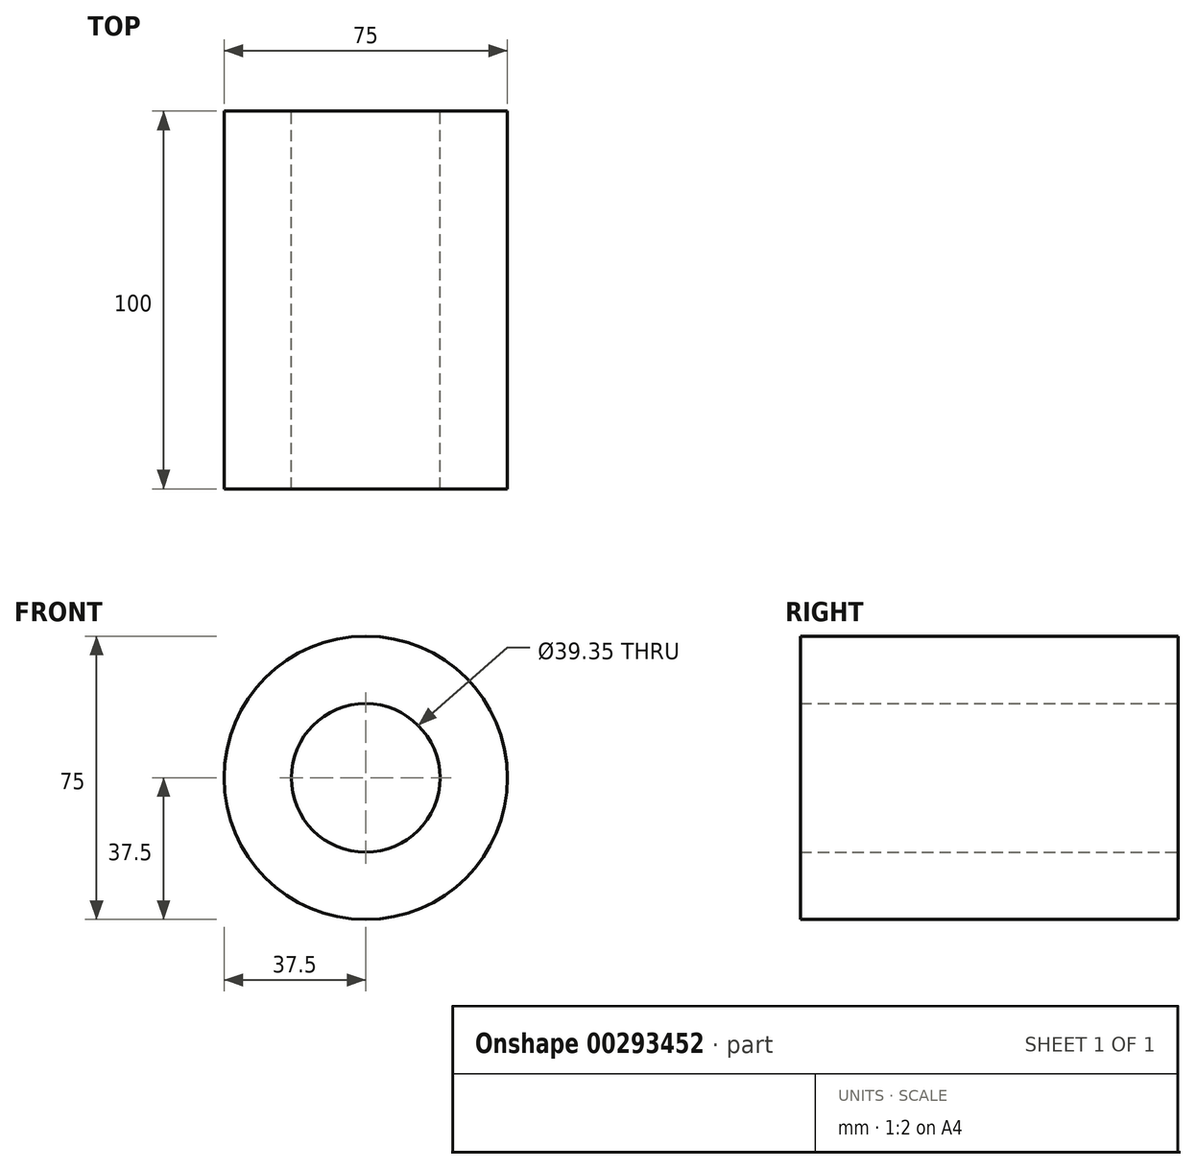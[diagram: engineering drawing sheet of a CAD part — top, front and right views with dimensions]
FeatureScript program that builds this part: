
annotation { "Feature Type Name" : "Feature", "Feature Type Description" : "" }
export const myFeature = defineFeature(function(context is Context, id is Id, definition is map)
    precondition{}
    {
        {
            var Q0;
            Q0=qCreatedBy(makeId("Front.planeOp"),FACE);
            var sketch = newSketch(context, id + "F0", { "sketchPlane" : qUnion([Q0])});
            skCircle(sketch, "E0", {"center": v(0, 0) * mm, "radius": 37.5 * mm});
            skCircle(sketch, "E1", {"center": v(0, 0) * mm, "radius": 19.68 * mm});
            skSolve(sketch);
        }
        {
            var Q0;
            Q0=makeQuery(id+"F0.imprint","IMPRINT",FACE,{"disambiguationData":[TD([[makeQuery(id+"F0.imprint","IMPRINT",EDGE,{"derivedFrom":sQuery(id+"F0.wireOp",EDGE,"E0")}),1.0]])]});
            extrude(context, id + "F1", {"entities" : qUnion([Q0]), "depth" : 100 * mm});
        }
    });
